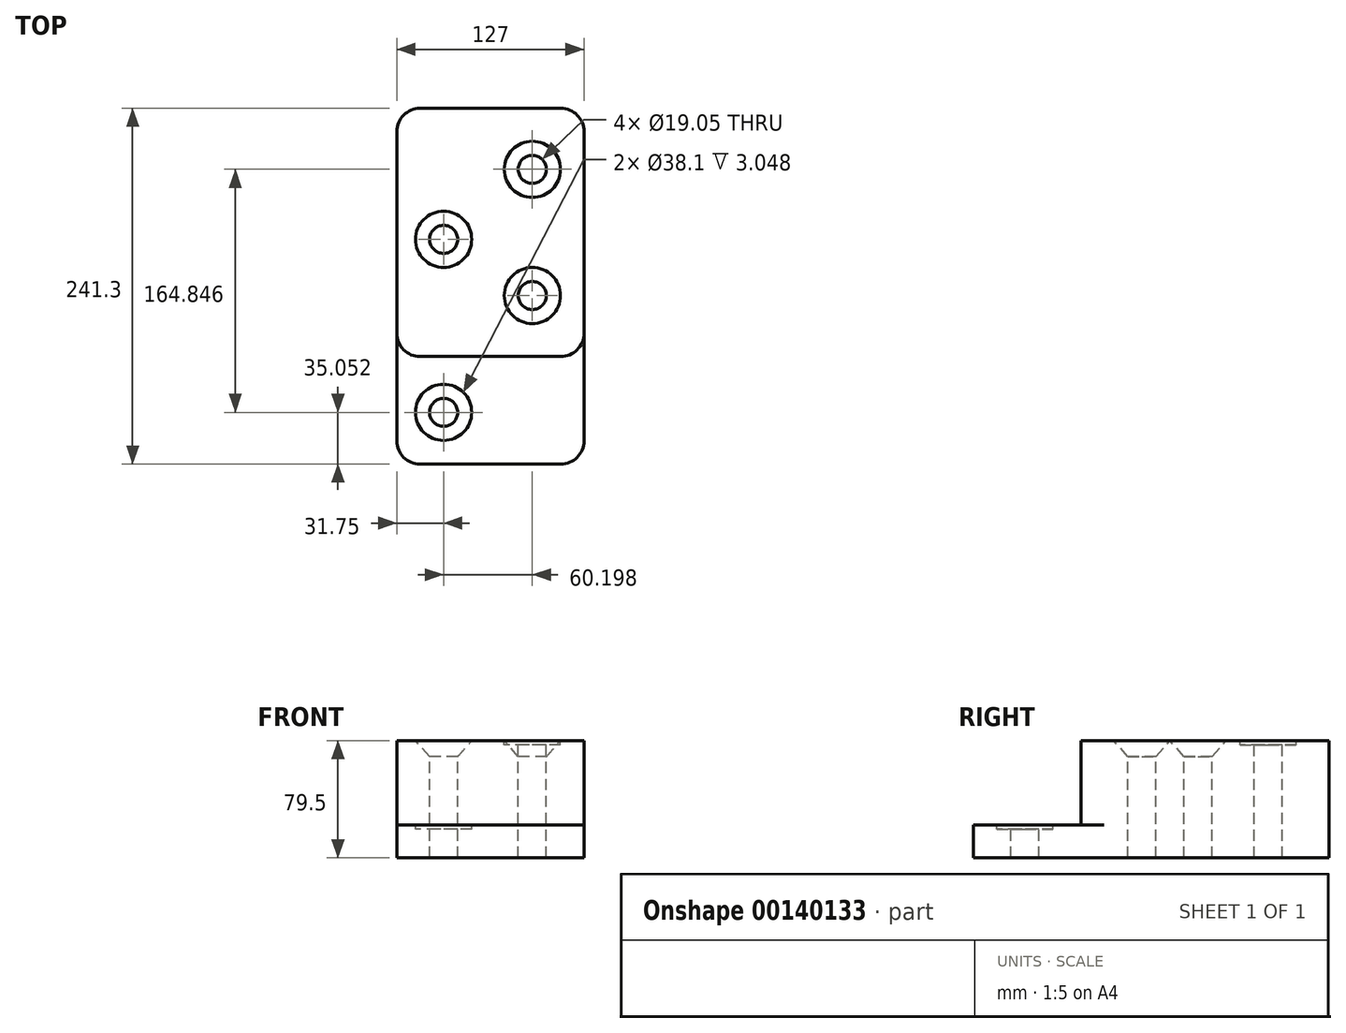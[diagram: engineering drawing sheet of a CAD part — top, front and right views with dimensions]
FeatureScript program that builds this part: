
annotation { "Feature Type Name" : "Feature", "Feature Type Description" : "" }
export const myFeature = defineFeature(function(context is Context, id is Id, definition is map)
    precondition{}
    {
        {
            var Q0;
            Q0=qCreatedBy(makeId("Top.planeOp"),FACE);
            var sketch = newSketch(context, id + "F0", { "sketchPlane" : qUnion([Q0])});
            skLineSegment(sketch, "E0.bottom", {"start": v(0, 0) * mm, "end": v(127, 0) * mm});
            skLineSegment(sketch, "E0.top", {"start": v(0, -168.4) * mm, "end": v(127, -168.4) * mm});
            skLineSegment(sketch, "E0.left", {"start": v(0, 0) * mm, "end": v(0, -168.4) * mm});
            skLineSegment(sketch, "E0.right", {"start": v(127, 0) * mm, "end": v(127, -168.4) * mm});
            skSolve(sketch);
        }
        {
            var Q0;
            Q0 = qSketchRegion(id + "F0", true);
            extrude(context, id + "F1", {"entities" : qUnion([Q0]), "depth" : 79.5 * mm});
        }
        {
            var Q0;
            Q0=makeQuery(id+"F1.opExtrude","CAP_FACE",FACE,{"disambiguationData":[OSD([sQuery(id+"F0.wireOp",EDGE,"E0.bottom"),sQuery(id+"F0.wireOp",EDGE,"E0.top"),sQuery(id+"F0.wireOp",EDGE,"E0.left"),sQuery(id+"F0.wireOp",EDGE,"E0.right")])],"isStart":true});
            var sketch = newSketch(context, id + "F2", { "sketchPlane" : qUnion([Q0])});
            skLineSegment(sketch, "E1.0", {"start": v(0, 168.4) * mm, "end": v(127, 168.4) * mm});
            skLineSegment(sketch, "E2", {"start": v(127, 168.4) * mm, "end": v(127, 241.3) * mm});
            skLineSegment(sketch, "E3", {"start": v(127, 241.3) * mm, "end": v(0, 241.3) * mm});
            skLineSegment(sketch, "E4", {"start": v(0, 241.3) * mm, "end": v(0, 168.4) * mm});
            skSolve(sketch);
        }
        {
            var Q0;
            Q0 = qSketchRegion(id + "F2", true);
            extrude(context, id + "F3", {"entities" : qUnion([Q0]), "operationType" : NewBodyOperationType.ADD, "oppositeDirection" : true, "depth" : 22.35 * mm});
        }
        {
            var Q0;
            Q0=makeQuery(id+"F3.opExtrude","SWEPT_EDGE",EDGE,{"disambiguationData":[OSD([sQuery(id+"F2.wireOp",EDGE,"E2"),sQuery(id+"F2.wireOp",EDGE,"E3")])]});
            var Q1;
            Q1=makeQuery(id+"F3.opExtrude","SWEPT_EDGE",EDGE,{"disambiguationData":[OSD([sQuery(id+"F2.wireOp",EDGE,"E3"),sQuery(id+"F2.wireOp",EDGE,"E4")])]});
            var Q2;
            Q2=makeQuery(id+"F1.opExtrude","SWEPT_EDGE",EDGE,{"disambiguationData":[OSD([sQuery(id+"F0.wireOp",EDGE,"E0.top"),sQuery(id+"F0.wireOp",EDGE,"E0.left")])]});
            var Q3;
            Q3=makeQuery(id+"F1.opExtrude","SWEPT_EDGE",EDGE,{"disambiguationData":[OSD([sQuery(id+"F0.wireOp",EDGE,"E0.top"),sQuery(id+"F0.wireOp",EDGE,"E0.right")])]});
            var Q4;
            Q4=makeQuery(id+"F1.opExtrude","SWEPT_EDGE",EDGE,{"disambiguationData":[OSD([sQuery(id+"F0.wireOp",EDGE,"E0.bottom"),sQuery(id+"F0.wireOp",EDGE,"E0.left")])]});
            var Q5;
            Q5=makeQuery(id+"F1.opExtrude","SWEPT_EDGE",EDGE,{"disambiguationData":[OSD([sQuery(id+"F0.wireOp",EDGE,"E0.bottom"),sQuery(id+"F0.wireOp",EDGE,"E0.right")])]});
            fillet(context, id + "F4", {"entities" : qUnion([Q0, Q1, Q2, Q3, Q4, Q5]), "radius" : 15.75 * mm, "tangentPropagation" : true, "allowEdgeOverflow" : false});
        }
        {
            var Q0;
            Q0=makeQuery(id+"F1.opExtrude","CAP_FACE",FACE,{"disambiguationData":[OSD([sQuery(id+"F0.wireOp",EDGE,"E0.bottom"),sQuery(id+"F0.wireOp",EDGE,"E0.top"),sQuery(id+"F0.wireOp",EDGE,"E0.left"),sQuery(id+"F0.wireOp",EDGE,"E0.right")])],"isStart":false});
            var sketch = newSketch(context, id + "F5", { "sketchPlane" : qUnion([Q0])});
            skPoint(sketch, "E5", {"position": v(31.75, -88.9) * mm});
            skPoint(sketch, "E6", {"position": v(91.95, -41.4) * mm});
            skPoint(sketch, "E7", {"position": v(91.95, -127) * mm});
            skPoint(sketch, "E8", {"position": v(31.75, -206.25) * mm});
            skSolve(sketch);
        }
        {
            var Q0;
            Q0=makeQuery(id+"F3.opExtrude","CAP_FACE",FACE,{"disambiguationData":[OSD([sQuery(id+"F2.wireOp",EDGE,"E1.0"),sQuery(id+"F2.wireOp",EDGE,"E2"),sQuery(id+"F2.wireOp",EDGE,"E3"),sQuery(id+"F2.wireOp",EDGE,"E4")])],"isStart":false});
            var sketch = newSketch(context, id + "F6", { "sketchPlane" : qUnion([Q0])});
            skPoint(sketch, "E9.0", {"position": v(31.75, -206.25) * mm});
            skSolve(sketch);
        }
        {
            var Q0;
            Q0=sQuery(id+"F5.wireOp",VERTEX,"E5");
            var Q1;
            Q1=sQuery(id+"F5.wireOp",VERTEX,"E7");
            var Q2;
            Q2=makeQuery(id+"F1.opExtrude","SWEPT_BODY",BODY,{"disambiguationData":[OSD([sQuery(id+"F0.wireOp",EDGE,"E0.bottom"),sQuery(id+"F0.wireOp",EDGE,"E0.top"),sQuery(id+"F0.wireOp",EDGE,"E0.left"),sQuery(id+"F0.wireOp",EDGE,"E0.right")])]});
            hole(context, id + "F7", {"style" : HoleStyle.C_SINK, "endStyle" : HoleEndStyle.THROUGH, "holeDiameter" : 19.05 * mm, "cSinkDiameter" : 38.1 * mm, "cSinkAngle" : 82 * degree, "locations" : qUnion([Q0, Q1]), "scope" : qUnion([Q2]), "isTappedThrough" : true});
        }
        {
            var Q0;
            Q0=sQuery(id+"F5.wireOp",VERTEX,"E6");
            var Q1;
            Q1=sQuery(id+"F6.wireOp",VERTEX,"E9.0");
            var Q2;
            Q2=makeQuery(id+"F1.opExtrude","SWEPT_BODY",BODY,{"disambiguationData":[OSD([sQuery(id+"F0.wireOp",EDGE,"E0.bottom"),sQuery(id+"F0.wireOp",EDGE,"E0.top"),sQuery(id+"F0.wireOp",EDGE,"E0.left"),sQuery(id+"F0.wireOp",EDGE,"E0.right")])]});
            hole(context, id + "F8", {"style" : HoleStyle.C_BORE, "endStyle" : HoleEndStyle.THROUGH, "holeDiameter" : 19.05 * mm, "cBoreDiameter" : 38.1 * mm, "cBoreDepth" : 3.05 * mm, "locations" : qUnion([Q0, Q1]), "scope" : qUnion([Q2]), "isTappedThrough" : true});
        }
    });
